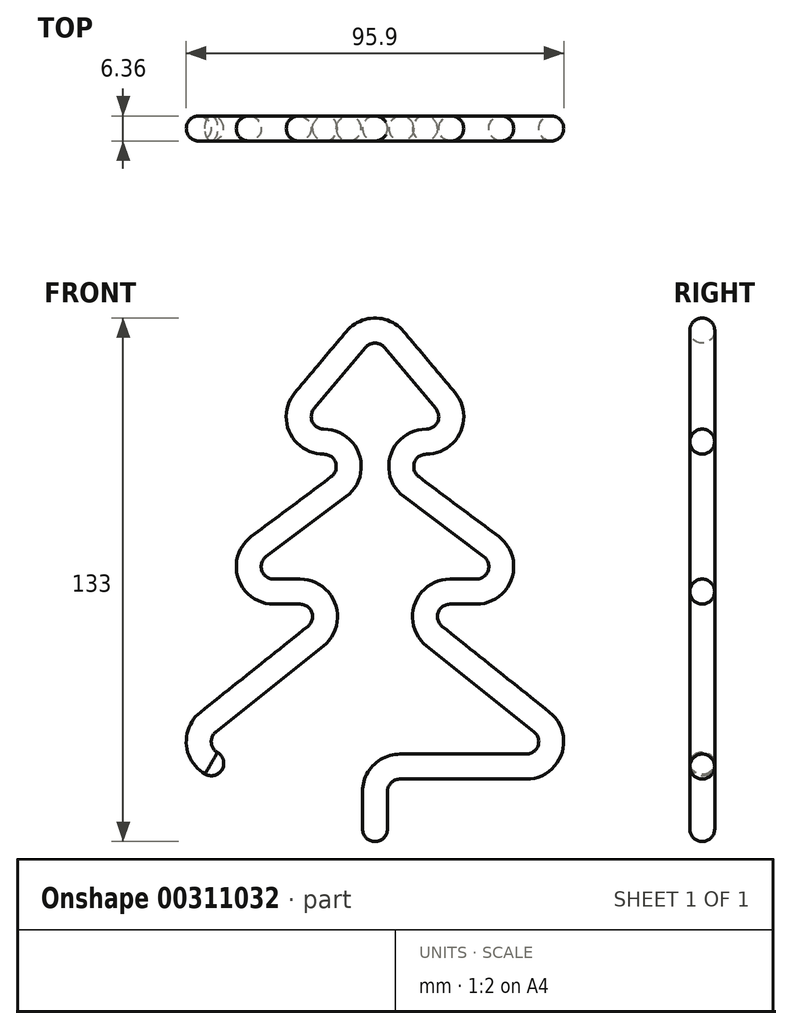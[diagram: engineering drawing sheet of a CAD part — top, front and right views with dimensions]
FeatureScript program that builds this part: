
annotation { "Feature Type Name" : "Feature", "Feature Type Description" : "" }
export const myFeature = defineFeature(function(context is Context, id is Id, definition is map)
    precondition{}
    {
        {
            var Q0;
            Q0=qCreatedBy(makeId("Front.planeOp"),FACE);
            var sketch = newSketch(context, id + "F0", { "sketchPlane" : qUnion([Q0])});
            skLineSegment(sketch, "E0", {"start": v(0, 0) * mm, "end": v(0, 12.7) * mm});
            skLineSegment(sketch, "E1", {"start": v(6.35, 19.05) * mm, "end": v(38.42, 19.05) * mm});
            skLineSegment(sketch, "E2", {"start": v(42.39, 30.36) * mm, "end": v(15.08, 52.2) * mm});
            skLineSegment(sketch, "E3", {"start": v(19.05, 63.5) * mm, "end": v(25.72, 63.5) * mm});
            skLineSegment(sketch, "E4", {"start": v(29.53, 74.93) * mm, "end": v(9.21, 90.17) * mm});
            skLineSegment(sketch, "E5", {"start": v(13.02, 101.6) * mm, "end": v(13.02, 101.6) * mm});
            skArc(sketch, "E6", {"start": v(38.42, 19.05) * mm, "mid": v(44.42, 23.3) * mm, "end": v(42.39, 30.36) * mm});
            skArc(sketch, "E7", {"start": v(25.72, 63.5) * mm, "mid": v(31.75, 67.84) * mm, "end": v(29.53, 74.93) * mm});
            skArc(sketch, "E8", {"start": v(13.02, 101.6) * mm, "mid": v(18.78, 105.27) * mm, "end": v(17.89, 112.03) * mm});
            skLineSegment(sketch, "E9", {"start": v(17.89, 112.03) * mm, "end": v(4.86, 127.55) * mm});
            skLineSegment(sketch, "E10", {"start": v(0, 133.35) * mm, "end": v(0, 101.6) * mm, "construction": true});
            skArc(sketch, "E11", {"start": v(19.05, 63.5) * mm, "mid": v(13.06, 59.25) * mm, "end": v(15.08, 52.2) * mm});
            skArc(sketch, "E12", {"start": v(13.02, 101.6) * mm, "mid": v(7, 97.26) * mm, "end": v(9.21, 90.17) * mm});
            skArc(sketch, "E13", {"start": v(6.35, 19.05) * mm, "mid": v(1.86, 17.2) * mm, "end": v(0, 12.7) * mm});
            skPoint(sketch, "E14.orphan", {"position": v(0, 19.05) * mm});
            skArc(sketch, "E15.MirrorCS", {"start": v(-13.02, 101.6) * mm, "mid": v(-7, 97.26) * mm, "end": v(-9.21, 90.17) * mm});
            skLineSegment(sketch, "E16.MirrorCS", {"start": v(-29.53, 74.93) * mm, "end": v(-9.21, 90.17) * mm});
            skArc(sketch, "E17.MirrorCS", {"start": v(-25.72, 63.5) * mm, "mid": v(-31.75, 67.84) * mm, "end": v(-29.53, 74.93) * mm});
            skLineSegment(sketch, "E18.MirrorCS", {"start": v(-19.05, 63.5) * mm, "end": v(-25.72, 63.5) * mm});
            skArc(sketch, "E19.MirrorCS", {"start": v(-19.05, 63.5) * mm, "mid": v(-13.06, 59.25) * mm, "end": v(-15.08, 52.2) * mm});
            skLineSegment(sketch, "E20.MirrorCS", {"start": v(-42.39, 30.36) * mm, "end": v(-15.08, 52.2) * mm});
            skArc(sketch, "E21.MirrorCS", {"start": v(-38.42, 19.05) * mm, "mid": v(-44.42, 23.3) * mm, "end": v(-42.39, 30.36) * mm});
            skArc(sketch, "E22", {"start": v(4.86, 127.55) * mm, "mid": v(0, 129.82) * mm, "end": v(-4.86, 127.55) * mm});
            skLineSegment(sketch, "E23.MirrorCS", {"start": v(-17.89, 112.03) * mm, "end": v(-4.86, 127.55) * mm});
            skArc(sketch, "E24.MirrorCS", {"start": v(-13.02, 101.6) * mm, "mid": v(-18.78, 105.27) * mm, "end": v(-17.89, 112.03) * mm});
            skSolve(sketch);
        }
        {
            var Q0;
            Q0=qCreatedBy(makeId("Top.planeOp"),FACE);
            var sketch = newSketch(context, id + "F1", { "sketchPlane" : qUnion([Q0])});
            skCircle(sketch, "E25", {"center": v(0, 0) * mm, "radius": 3.18 * mm});
            skSolve(sketch);
        }
        {
            var Q0;
            Q0=makeQuery(id+"F1.imprint","IMPRINT",FACE,{"disambiguationData":[TD([[makeQuery(id+"F1.imprint","IMPRINT",EDGE,{"derivedFrom":sQuery(id+"F1.wireOp",EDGE,"E25")}),1.0]])]});
            var Q1;
            Q1 = qConstructionFilter(qBodyType(qCreatedBy(id + "F0" ,EDGE), BodyType.WIRE), ConstructionObject.NO);
            sweep(context, id + "F2", {"profiles" : qUnion([Q0]), "path" : qUnion([Q1])});
        }
        {
            var Q0;
            Q0=makeQuery(id+"F2.opSweep","CAP_EDGE",EDGE,{"disambiguationData":[OSD([sQuery(id+"F0.wireOp",VERTEX,"udPUMviU-vKOM-feQZ-svGP-w1x00g2ICois.end"),sQuery(id+"F1.wireOp",EDGE,"E25")])],"isStart":false});
            var Q1;
            Q1=makeQuery(id+"F2.opSweep","CAP_EDGE",EDGE,{"disambiguationData":[OSD([sQuery(id+"F0.wireOp",VERTEX,"E0.start"),sQuery(id+"F1.wireOp",EDGE,"E25")])],"isStart":true});
            fillet(context, id + "F3", {"entities" : qUnion([Q0, Q1]), "radius" : 3.17 * mm, "tangentPropagation" : true, "allowEdgeOverflow" : false});
        }
    });
